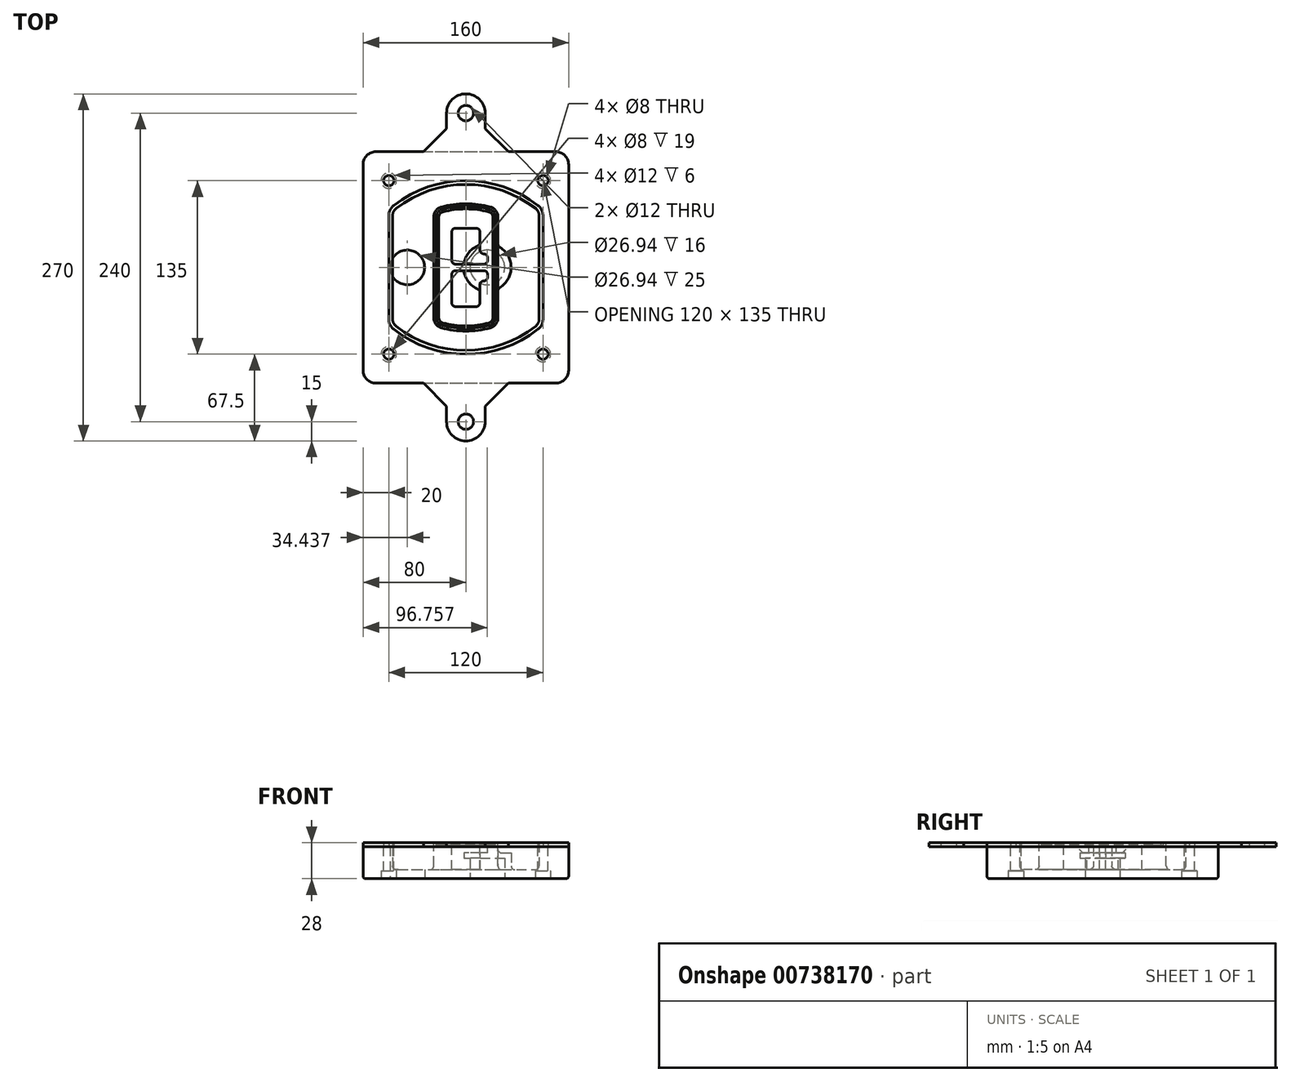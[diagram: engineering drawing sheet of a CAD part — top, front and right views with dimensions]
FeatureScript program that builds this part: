
annotation { "Feature Type Name" : "Feature", "Feature Type Description" : "" }
export const myFeature = defineFeature(function(context is Context, id is Id, definition is map)
    precondition{}
    {
        {
            var Q0;
            Q0=qCreatedBy(makeId("Top.planeOp"),FACE);
            var sketch = newSketch(context, id + "F0", { "sketchPlane" : qUnion([Q0])});
            skPoint(sketch, "E0.rect.middle", {"position": v(0, 0) * mm});
            skLineSegment(sketch, "E1.bottom", {"start": v(-70, -90) * mm, "end": v(70, -90) * mm});
            skLineSegment(sketch, "E1.top", {"start": v(-70, 90) * mm, "end": v(70, 90) * mm});
            skLineSegment(sketch, "E1.left", {"start": v(-80, -80) * mm, "end": v(-80, 80) * mm});
            skLineSegment(sketch, "E1.right", {"start": v(80, -80) * mm, "end": v(80, 80) * mm});
            skLineSegment(sketch, "E2", {"start": v(-80, 90) * mm, "end": v(80, -90) * mm, "construction": true});
            skLineSegment(sketch, "E3", {"start": v(80, 90) * mm, "end": v(-80, -90) * mm, "construction": true});
            skCircle(sketch, "E4", {"center": v(-60, 67.5) * mm, "radius": 4 * mm});
            skCircle(sketch, "E5", {"center": v(60, 67.5) * mm, "radius": 4 * mm});
            skCircle(sketch, "E6", {"center": v(60, -67.5) * mm, "radius": 4 * mm});
            skCircle(sketch, "E7", {"center": v(-60, -67.5) * mm, "radius": 4 * mm});
            skLineSegment(sketch, "E8", {"start": v(-60, 67.5) * mm, "end": v(60, 67.5) * mm, "construction": true});
            skLineSegment(sketch, "E9", {"start": v(60, 67.5) * mm, "end": v(60, -67.5) * mm, "construction": true});
            skLineSegment(sketch, "E10", {"start": v(60, -67.5) * mm, "end": v(-60, -67.5) * mm, "construction": true});
            skLineSegment(sketch, "E11", {"start": v(-60, -67.5) * mm, "end": v(-60, 67.5) * mm, "construction": true});
            skLineSegment(sketch, "E12", {"start": v(-60, 40.3) * mm, "end": v(-60, -40.3) * mm});
            skLineSegment(sketch, "E13", {"start": v(60, 40.3) * mm, "end": v(60, -40.3) * mm});
            skArc(sketch, "E14", {"start": v(56.15, 48.18) * mm, "mid": v(0, 67.5) * mm, "end": v(-56.15, 48.18) * mm});
            skArc(sketch, "E15", {"start": v(-56.15, -48.18) * mm, "mid": v(0, -67.5) * mm, "end": v(56.15, -48.18) * mm});
            skLineSegment(sketch, "E16", {"start": v(-60, 0) * mm, "end": v(60, 0) * mm, "construction": true});
            skPoint(sketch, "E17.visualSharp", {"position": v(-60, -45) * mm});
            skArc(sketch, "E17.filletArc", {"start": v(-60, -40.3) * mm, "mid": v(-58.99, -44.68) * mm, "end": v(-56.15, -48.18) * mm});
            skPoint(sketch, "E18.visualSharp", {"position": v(-60, 45) * mm});
            skArc(sketch, "E18.filletArc", {"start": v(-56.15, 48.18) * mm, "mid": v(-58.99, 44.68) * mm, "end": v(-60, 40.3) * mm});
            skPoint(sketch, "E19.visualSharp", {"position": v(60, 45) * mm});
            skArc(sketch, "E19.filletArc", {"start": v(60, 40.3) * mm, "mid": v(58.99, 44.68) * mm, "end": v(56.15, 48.18) * mm});
            skPoint(sketch, "E20.visualSharp", {"position": v(60, -45) * mm});
            skArc(sketch, "E20.filletArc", {"start": v(56.15, -48.18) * mm, "mid": v(58.99, -44.68) * mm, "end": v(60, -40.3) * mm});
            skPoint(sketch, "E21.visualSharp", {"position": v(-80, 90) * mm});
            skArc(sketch, "E21.filletArc", {"start": v(-70, 90) * mm, "mid": v(-77.07, 87.07) * mm, "end": v(-80, 80) * mm});
            skPoint(sketch, "E22.visualSharp", {"position": v(80, 90) * mm});
            skArc(sketch, "E22.filletArc", {"start": v(80, 80) * mm, "mid": v(77.07, 87.07) * mm, "end": v(70, 90) * mm});
            skPoint(sketch, "E23.visualSharp", {"position": v(80, -90) * mm});
            skArc(sketch, "E23.filletArc", {"start": v(70, -90) * mm, "mid": v(77.07, -87.07) * mm, "end": v(80, -80) * mm});
            skPoint(sketch, "E24.visualSharp", {"position": v(-80, -90) * mm});
            skArc(sketch, "E24.filletArc", {"start": v(-80, -80) * mm, "mid": v(-77.07, -87.07) * mm, "end": v(-70, -90) * mm});
            skArc(sketch, "E25.0", {"start": v(57, 40.3) * mm, "mid": v(56.3, 43.36) * mm, "end": v(54.3, 45.81) * mm});
            skLineSegment(sketch, "E25.1", {"start": v(57, 40.3) * mm, "end": v(57, -40.3) * mm});
            skArc(sketch, "E25.2", {"start": v(54.3, -45.81) * mm, "mid": v(56.3, -43.36) * mm, "end": v(57, -40.3) * mm});
            skArc(sketch, "E25.3", {"start": v(-54.3, -45.81) * mm, "mid": v(0, -64.5) * mm, "end": v(54.3, -45.81) * mm});
            skArc(sketch, "E25.4", {"start": v(-57, -40.3) * mm, "mid": v(-56.3, -43.36) * mm, "end": v(-54.3, -45.81) * mm});
            skArc(sketch, "E25.5", {"start": v(54.3, 45.81) * mm, "mid": v(0, 64.5) * mm, "end": v(-54.3, 45.81) * mm});
            skLineSegment(sketch, "E25.6", {"start": v(-57, 40.3) * mm, "end": v(-57, -40.3) * mm});
            skArc(sketch, "E25.7", {"start": v(-54.3, 45.81) * mm, "mid": v(-56.3, 43.36) * mm, "end": v(-57, 40.3) * mm});
            skArc(sketch, "E26.0", {"start": v(-58.62, 51.33) * mm, "mid": v(-62.58, 46.43) * mm, "end": v(-64, 40.3) * mm});
            skArc(sketch, "E26.1", {"start": v(58.62, 51.33) * mm, "mid": v(0, 71.5) * mm, "end": v(-58.62, 51.33) * mm});
            skArc(sketch, "E26.2", {"start": v(64, 40.3) * mm, "mid": v(62.58, 46.43) * mm, "end": v(58.62, 51.33) * mm});
            skLineSegment(sketch, "E26.3", {"start": v(64, 40.3) * mm, "end": v(64, -40.3) * mm});
            skArc(sketch, "E26.4", {"start": v(58.62, -51.33) * mm, "mid": v(62.58, -46.43) * mm, "end": v(64, -40.3) * mm});
            skLineSegment(sketch, "E26.5", {"start": v(-64, 40.3) * mm, "end": v(-64, -40.3) * mm});
            skArc(sketch, "E26.6", {"start": v(-58.62, -51.33) * mm, "mid": v(0, -71.5) * mm, "end": v(58.62, -51.33) * mm});
            skArc(sketch, "E26.7", {"start": v(-64, -40.3) * mm, "mid": v(-62.58, -46.43) * mm, "end": v(-58.62, -51.33) * mm});
            skSolve(sketch);
        }
        {
            var Q0;
            Q0=makeQuery(id+"F0.imprint","IMPRINT",FACE,{"disambiguationData":[TD([[makeQuery(id+"F0.imprint","IMPRINT",EDGE,{"derivedFrom":sQuery(id+"F0.wireOp",EDGE,"E1.bottom")}),1.0]])]});
            var Q1;
            Q1=makeQuery(id+"F0.imprint","IMPRINT",FACE,{"disambiguationData":[TD([[makeQuery(id+"F0.imprint","IMPRINT",EDGE,{"derivedFrom":sQuery(id+"F0.wireOp",EDGE,"E12")}),1.0]])]});
            var Q2;
            Q2=makeQuery(id+"F0.imprint","IMPRINT",FACE,{"disambiguationData":[TD([[makeQuery(id+"F0.imprint","IMPRINT",EDGE,{"derivedFrom":sQuery(id+"F0.wireOp",EDGE,"E25.0")}),1.0]])]});
            var Q3;
            Q3=makeQuery(id+"F0.imprint","IMPRINT",FACE,{"disambiguationData":[TD([[makeQuery(id+"F0.imprint","IMPRINT",EDGE,{"derivedFrom":sQuery(id+"F0.wireOp",EDGE,"E12")}),-1.0]])]});
            extrude(context, id + "F1", {"entities" : qUnion([Q0, Q1, Q2, Q3]), "oppositeDirection" : true, "depth" : 25 * mm});
        }
        {
            var Q0;
            Q0=makeQuery(id+"F0.imprint","IMPRINT",FACE,{"disambiguationData":[TD([[makeQuery(id+"F0.imprint","IMPRINT",EDGE,{"derivedFrom":sQuery(id+"F0.wireOp",EDGE,"E12")}),1.0]])]});
            extrude(context, id + "F2", {"entities" : qUnion([Q0]), "operationType" : NewBodyOperationType.ADD, "depth" : 3 * mm, "offsetDistance" : 25 * mm});
        }
        {
            var Q0;
            Q0=makeQuery(id+"F0.imprint","IMPRINT",FACE,{"disambiguationData":[TD([[makeQuery(id+"F0.imprint","IMPRINT",EDGE,{"derivedFrom":sQuery(id+"F0.wireOp",EDGE,"E25.0")}),1.0]])]});
            extrude(context, id + "F3", {"entities" : qUnion([Q0]), "operationType" : NewBodyOperationType.REMOVE, "oppositeDirection" : true, "depth" : 18 * mm});
        }
        {
            var Q0;
            Q0=makeQuery(id+"F2.opExtrude","CAP_FACE",FACE,{"disambiguationData":[OSD([sQuery(id+"F0.wireOp",EDGE,"E12"),sQuery(id+"F0.wireOp",EDGE,"E13"),sQuery(id+"F0.wireOp",EDGE,"E14"),sQuery(id+"F0.wireOp",EDGE,"E15"),sQuery(id+"F0.wireOp",EDGE,"E17.filletArc"),sQuery(id+"F0.wireOp",EDGE,"E18.filletArc"),sQuery(id+"F0.wireOp",EDGE,"E19.filletArc"),sQuery(id+"F0.wireOp",EDGE,"E20.filletArc"),sQuery(id+"F0.wireOp",EDGE,"E25.0"),sQuery(id+"F0.wireOp",EDGE,"E25.1"),sQuery(id+"F0.wireOp",EDGE,"E25.2"),sQuery(id+"F0.wireOp",EDGE,"E25.3"),sQuery(id+"F0.wireOp",EDGE,"E25.4"),sQuery(id+"F0.wireOp",EDGE,"E25.5"),sQuery(id+"F0.wireOp",EDGE,"E25.6"),sQuery(id+"F0.wireOp",EDGE,"E25.7")])],"isStart":false});
            var sketch = newSketch(context, id + "F4", { "sketchPlane" : qUnion([Q0])});
            skArc(sketch, "E27.0", {"start": v(-19.08, -46.97) * mm, "mid": v(0, -49.5) * mm, "end": v(19.08, -46.97) * mm});
            skArc(sketch, "E28.0", {"start": v(19.08, 46.97) * mm, "mid": v(0, 49.5) * mm, "end": v(-19.08, 46.97) * mm});
            skLineSegment(sketch, "E29", {"start": v(-25, 39.25) * mm, "end": v(-25, -39.25) * mm});
            skLineSegment(sketch, "E30", {"start": v(25, 39.25) * mm, "end": v(25, -39.25) * mm});
            skLineSegment(sketch, "E31", {"start": v(-25, 45.1) * mm, "end": v(25, 45.1) * mm, "construction": true});
            skLineSegment(sketch, "E32", {"start": v(-25, -45.1) * mm, "end": v(25, -45.1) * mm, "construction": true});
            skPoint(sketch, "E33.visualSharp", {"position": v(-25, 45.1) * mm});
            skArc(sketch, "E33.filletArc", {"start": v(-19.08, 46.97) * mm, "mid": v(-23.35, 44.11) * mm, "end": v(-25, 39.25) * mm});
            skPoint(sketch, "E34.visualSharp", {"position": v(25, 45.1) * mm});
            skArc(sketch, "E34.filletArc", {"start": v(25, 39.25) * mm, "mid": v(23.35, 44.11) * mm, "end": v(19.08, 46.97) * mm});
            skPoint(sketch, "E35.visualSharp", {"position": v(25, -45.1) * mm});
            skArc(sketch, "E35.filletArc", {"start": v(19.08, -46.97) * mm, "mid": v(23.35, -44.11) * mm, "end": v(25, -39.25) * mm});
            skPoint(sketch, "E36.visualSharp", {"position": v(-25, -45.1) * mm});
            skArc(sketch, "E36.filletArc", {"start": v(-25, -39.25) * mm, "mid": v(-23.35, -44.11) * mm, "end": v(-19.08, -46.97) * mm});
            skArc(sketch, "E37.0", {"start": v(54.3, 45.81) * mm, "mid": v(0, 64.5) * mm, "end": v(-54.3, 45.81) * mm});
            skArc(sketch, "E37.1", {"start": v(-54.3, 45.81) * mm, "mid": v(-56.3, 43.36) * mm, "end": v(-57, 40.3) * mm});
            skLineSegment(sketch, "E37.2", {"start": v(-57, 40.3) * mm, "end": v(-57, -40.3) * mm});
            skArc(sketch, "E37.3", {"start": v(-57, -40.3) * mm, "mid": v(-56.3, -43.36) * mm, "end": v(-54.3, -45.81) * mm});
            skArc(sketch, "E37.4", {"start": v(-54.3, -45.81) * mm, "mid": v(0, -64.5) * mm, "end": v(54.3, -45.81) * mm});
            skArc(sketch, "E37.5", {"start": v(54.3, -45.81) * mm, "mid": v(56.3, -43.36) * mm, "end": v(57, -40.3) * mm});
            skLineSegment(sketch, "E37.6", {"start": v(57, 40.3) * mm, "end": v(57, -40.3) * mm});
            skArc(sketch, "E37.7", {"start": v(57, 40.3) * mm, "mid": v(56.3, 43.36) * mm, "end": v(54.3, 45.81) * mm});
            skLineSegment(sketch, "E38.0", {"start": v(23, 39.25) * mm, "end": v(23, -39.25) * mm});
            skArc(sketch, "E38.1", {"start": v(18.56, -45.04) * mm, "mid": v(21.76, -42.9) * mm, "end": v(23, -39.25) * mm});
            skArc(sketch, "E38.2", {"start": v(-18.56, -45.04) * mm, "mid": v(0, -47.5) * mm, "end": v(18.56, -45.04) * mm});
            skArc(sketch, "E38.3", {"start": v(-23, -39.25) * mm, "mid": v(-21.76, -42.9) * mm, "end": v(-18.56, -45.04) * mm});
            skLineSegment(sketch, "E38.4", {"start": v(-23, 39.25) * mm, "end": v(-23, -39.25) * mm});
            skArc(sketch, "E38.5", {"start": v(23, 39.25) * mm, "mid": v(21.76, 42.9) * mm, "end": v(18.56, 45.04) * mm});
            skArc(sketch, "E38.6", {"start": v(-18.56, 45.04) * mm, "mid": v(-21.76, 42.9) * mm, "end": v(-23, 39.25) * mm});
            skArc(sketch, "E38.7", {"start": v(18.56, 45.04) * mm, "mid": v(0, 47.5) * mm, "end": v(-18.56, 45.04) * mm});
            skArc(sketch, "E39.0", {"start": v(21, 39.25) * mm, "mid": v(20.18, 41.68) * mm, "end": v(18.04, 43.1) * mm});
            skLineSegment(sketch, "E39.1", {"start": v(21, 39.25) * mm, "end": v(21, -39.25) * mm});
            skArc(sketch, "E39.2", {"start": v(18.04, -43.1) * mm, "mid": v(20.18, -41.68) * mm, "end": v(21, -39.25) * mm});
            skArc(sketch, "E39.3", {"start": v(-18.04, -43.1) * mm, "mid": v(0, -45.5) * mm, "end": v(18.04, -43.1) * mm});
            skArc(sketch, "E39.4", {"start": v(-21, -39.25) * mm, "mid": v(-20.18, -41.68) * mm, "end": v(-18.04, -43.1) * mm});
            skArc(sketch, "E39.5", {"start": v(18.04, 43.1) * mm, "mid": v(0, 45.5) * mm, "end": v(-18.04, 43.1) * mm});
            skLineSegment(sketch, "E39.6", {"start": v(-21, 39.25) * mm, "end": v(-21, -39.25) * mm});
            skArc(sketch, "E39.7", {"start": v(-18.04, 43.1) * mm, "mid": v(-20.18, 41.68) * mm, "end": v(-21, 39.25) * mm});
            skLineSegment(sketch, "E40", {"start": v(-25, 0) * mm, "end": v(25, 0) * mm, "construction": true});
            skLineSegment(sketch, "E41", {"start": v(-11, 5.5) * mm, "end": v(-11, 27.5) * mm});
            skLineSegment(sketch, "E42", {"start": v(-8, 30.5) * mm, "end": v(8, 30.5) * mm});
            skLineSegment(sketch, "E43", {"start": v(11, 27.5) * mm, "end": v(11, 13.5) * mm});
            skLineSegment(sketch, "E44", {"start": v(14, 10.5) * mm, "end": v(14, 10.5) * mm});
            skLineSegment(sketch, "E45", {"start": v(17, 7.5) * mm, "end": v(17, 5.5) * mm});
            skLineSegment(sketch, "E46", {"start": v(14, 2.5) * mm, "end": v(-8, 2.5) * mm});
            skPoint(sketch, "E47.visualSharp", {"position": v(-11, 30.5) * mm});
            skArc(sketch, "E47.filletArc", {"start": v(-8, 30.5) * mm, "mid": v(-10.12, 29.62) * mm, "end": v(-11, 27.5) * mm});
            skPoint(sketch, "E48.visualSharp", {"position": v(11, 30.5) * mm});
            skArc(sketch, "E48.filletArc", {"start": v(11, 27.5) * mm, "mid": v(10.12, 29.62) * mm, "end": v(8, 30.5) * mm});
            skPoint(sketch, "E49.visualSharp", {"position": v(11, 10.5) * mm});
            skArc(sketch, "E49.filletArc", {"start": v(11, 13.5) * mm, "mid": v(11.88, 11.38) * mm, "end": v(14, 10.5) * mm});
            skPoint(sketch, "E50.visualSharp", {"position": v(17, 10.5) * mm});
            skArc(sketch, "E50.filletArc", {"start": v(17, 7.5) * mm, "mid": v(16.12, 9.62) * mm, "end": v(14, 10.5) * mm});
            skPoint(sketch, "E51.visualSharp", {"position": v(17, 2.5) * mm});
            skArc(sketch, "E51.filletArc", {"start": v(14, 2.5) * mm, "mid": v(16.12, 3.38) * mm, "end": v(17, 5.5) * mm});
            skPoint(sketch, "E52.visualSharp", {"position": v(-11, 2.5) * mm});
            skArc(sketch, "E52.filletArc", {"start": v(-11, 5.5) * mm, "mid": v(-10.12, 3.38) * mm, "end": v(-8, 2.5) * mm});
            skLineSegment(sketch, "E53.0.MirrorCS", {"start": v(14, -2.5) * mm, "end": v(-8, -2.5) * mm});
            skArc(sketch, "E54.0.MirrorCS", {"start": v(-11, -5.5) * mm, "mid": v(-10.12, -3.38) * mm, "end": v(-8, -2.5) * mm});
            skLineSegment(sketch, "E55.0.MirrorCS", {"start": v(-11, -5.5) * mm, "end": v(-11, -27.5) * mm});
            skArc(sketch, "E56.0.MirrorCS", {"start": v(-8, -30.5) * mm, "mid": v(-10.12, -29.62) * mm, "end": v(-11, -27.5) * mm});
            skLineSegment(sketch, "E57.0.MirrorCS", {"start": v(-8, -30.5) * mm, "end": v(8, -30.5) * mm});
            skArc(sketch, "E58.0.MirrorCS", {"start": v(11, -27.5) * mm, "mid": v(10.12, -29.62) * mm, "end": v(8, -30.5) * mm});
            skLineSegment(sketch, "E59.0.MirrorCS", {"start": v(11, -27.5) * mm, "end": v(11, -13.5) * mm});
            skArc(sketch, "E60.0.MirrorCS", {"start": v(11, -13.5) * mm, "mid": v(11.88, -11.38) * mm, "end": v(14, -10.5) * mm});
            skArc(sketch, "E61.0.MirrorCS", {"start": v(17, -7.5) * mm, "mid": v(16.12, -9.62) * mm, "end": v(14, -10.5) * mm});
            skLineSegment(sketch, "E62.0.MirrorCS", {"start": v(17, -7.5) * mm, "end": v(17, -5.5) * mm});
            skArc(sketch, "E63.0.MirrorCS", {"start": v(14, -2.5) * mm, "mid": v(16.12, -3.38) * mm, "end": v(17, -5.5) * mm});
            skSolve(sketch);
        }
        {
            var Q0;
            Q0=makeQuery(id+"F4.imprint","IMPRINT",FACE,{"disambiguationData":[TD([[makeQuery(id+"F4.imprint","IMPRINT",EDGE,{"derivedFrom":sQuery(id+"F4.wireOp",EDGE,"E27.0")}),1.0]])]});
            var Q1;
            Q1=makeQuery(id+"F4.imprint","IMPRINT",FACE,{"disambiguationData":[TD([[makeQuery(id+"F4.imprint","IMPRINT",EDGE,{"derivedFrom":sQuery(id+"F4.wireOp",EDGE,"E38.0")}),-1.0]])]});
            var Q2;
            Q2=makeQuery(id+"F4.imprint","IMPRINT",FACE,{"disambiguationData":[TD([[makeQuery(id+"F4.imprint","IMPRINT",EDGE,{"derivedFrom":sQuery(id+"F4.wireOp",EDGE,"E39.0")}),1.0]])]});
            extrude(context, id + "F5", {"entities" : qUnion([Q0, Q1, Q2]), "operationType" : NewBodyOperationType.ADD, "endBound" : BoundingType.UP_TO_NEXT, "oppositeDirection" : true, "depth" : 25 * mm});
        }
        {
            var Q0;
            Q0=makeQuery(id+"F4.imprint","IMPRINT",FACE,{"disambiguationData":[TD([[makeQuery(id+"F4.imprint","IMPRINT",EDGE,{"derivedFrom":sQuery(id+"F4.wireOp",EDGE,"E38.0")}),-1.0]])]});
            extrude(context, id + "F6", {"entities" : qUnion([Q0]), "operationType" : NewBodyOperationType.REMOVE, "oppositeDirection" : true, "depth" : 2 * mm});
        }
        {
            var Q0;
            Q0=makeQuery(id+"F1.opExtrude","CAP_FACE",FACE,{"disambiguationData":[OSD([sQuery(id+"F0.wireOp",EDGE,"E1.bottom"),sQuery(id+"F0.wireOp",EDGE,"E1.top"),sQuery(id+"F0.wireOp",EDGE,"E1.left"),sQuery(id+"F0.wireOp",EDGE,"E1.right"),sQuery(id+"F0.wireOp",EDGE,"E4"),sQuery(id+"F0.wireOp",EDGE,"E5"),sQuery(id+"F0.wireOp",EDGE,"E6"),sQuery(id+"F0.wireOp",EDGE,"E7"),sQuery(id+"F0.wireOp",EDGE,"E21.filletArc"),sQuery(id+"F0.wireOp",EDGE,"E22.filletArc"),sQuery(id+"F0.wireOp",EDGE,"E23.filletArc"),sQuery(id+"F0.wireOp",EDGE,"E24.filletArc")])],"isStart":false});
            var sketch = newSketch(context, id + "F7", { "sketchPlane" : qUnion([Q0])});
            skCircle(sketch, "E64", {"center": v(16.76, 0) * mm, "radius": 13.47 * mm});
            skCircle(sketch, "E65", {"center": v(-45.56, 0) * mm, "radius": 13.47 * mm});
            skLineSegment(sketch, "E66", {"start": v(80, 0) * mm, "end": v(-80, 0) * mm});
            skCircle(sketch, "E67", {"center": v(16.76, 0) * mm, "radius": 18.47 * mm});
            skCircle(sketch, "E68", {"center": v(60, -67.5) * mm, "radius": 6 * mm});
            skCircle(sketch, "E69", {"center": v(-60, -67.5) * mm, "radius": 6 * mm});
            skCircle(sketch, "E70", {"center": v(-60, 67.5) * mm, "radius": 6 * mm});
            skCircle(sketch, "E71", {"center": v(60, 67.5) * mm, "radius": 6 * mm});
            skSolve(sketch);
        }
        {
            var Q0;
            {var subQ1=sQuery(id+"F7.wireOp",EDGE,"E66");var subQ4=sQuery(id+"F7.wireOp",EDGE,"E64");var subQ6=makeQuery(id+"F7.imprint","INTERSECT",VERTEX,{"disambiguationData":[OD(0.0)],"derivedFrom":[subQ4,subQ1]});Q0=makeQuery(id+"F7.imprint","IMPRINT",FACE,{"disambiguationData":[TD([[makeQuery(id+"F7.imprint","IMPRINT",EDGE,{"disambiguationData":[TD([[subQ6,-1.0]])],"derivedFrom":subQ4}),-1.0]])]});}
            var Q1;
            {var subQ0=sQuery(id+"F7.wireOp",EDGE,"E66");var subQ1=sQuery(id+"F7.wireOp",EDGE,"E64");var subQ3=makeQuery(id+"F7.imprint","INTERSECT",VERTEX,{"disambiguationData":[OD(0.0)],"derivedFrom":[subQ1,subQ0]});Q1=makeQuery(id+"F7.imprint","IMPRINT",FACE,{"disambiguationData":[TD([[makeQuery(id+"F7.imprint","IMPRINT",EDGE,{"disambiguationData":[TD([[subQ3,-1.0]])],"derivedFrom":subQ1}),1.0]])]});}
            var Q2;
            {var subQ0=sQuery(id+"F7.wireOp",EDGE,"E66");var subQ1=sQuery(id+"F7.wireOp",EDGE,"E64");var subQ3=makeQuery(id+"F7.imprint","INTERSECT",VERTEX,{"disambiguationData":[OD(0.0)],"derivedFrom":[subQ1,subQ0]});Q2=makeQuery(id+"F7.imprint","IMPRINT",FACE,{"disambiguationData":[TD([[makeQuery(id+"F7.imprint","IMPRINT",EDGE,{"disambiguationData":[TD([[subQ3,1.0]])],"derivedFrom":subQ1}),1.0]])]});}
            var Q3;
            {var subQ1=sQuery(id+"F7.wireOp",EDGE,"E66");var subQ4=sQuery(id+"F7.wireOp",EDGE,"E64");var subQ6=makeQuery(id+"F7.imprint","INTERSECT",VERTEX,{"disambiguationData":[OD(0.0)],"derivedFrom":[subQ4,subQ1]});Q3=makeQuery(id+"F7.imprint","IMPRINT",FACE,{"disambiguationData":[TD([[makeQuery(id+"F7.imprint","IMPRINT",EDGE,{"disambiguationData":[TD([[subQ6,1.0]])],"derivedFrom":subQ4}),-1.0]])]});}
            extrude(context, id + "F8", {"entities" : qUnion([Q0, Q1, Q2, Q3]), "operationType" : NewBodyOperationType.ADD, "oppositeDirection" : true, "depth" : 20 * mm});
        }
        {
            var Q0;
            {var subQ0=sQuery(id+"F7.wireOp",EDGE,"E66");var subQ1=sQuery(id+"F7.wireOp",EDGE,"E64");var subQ3=makeQuery(id+"F7.imprint","INTERSECT",VERTEX,{"disambiguationData":[OD(0.0)],"derivedFrom":[subQ1,subQ0]});Q0=makeQuery(id+"F7.imprint","IMPRINT",FACE,{"disambiguationData":[TD([[makeQuery(id+"F7.imprint","IMPRINT",EDGE,{"disambiguationData":[TD([[subQ3,-1.0]])],"derivedFrom":subQ1}),1.0]])]});}
            var Q1;
            {var subQ0=sQuery(id+"F7.wireOp",EDGE,"E66");var subQ1=sQuery(id+"F7.wireOp",EDGE,"E64");var subQ3=makeQuery(id+"F7.imprint","INTERSECT",VERTEX,{"disambiguationData":[OD(0.0)],"derivedFrom":[subQ1,subQ0]});Q1=makeQuery(id+"F7.imprint","IMPRINT",FACE,{"disambiguationData":[TD([[makeQuery(id+"F7.imprint","IMPRINT",EDGE,{"disambiguationData":[TD([[subQ3,1.0]])],"derivedFrom":subQ1}),1.0]])]});}
            extrude(context, id + "F9", {"entities" : qUnion([Q0, Q1]), "operationType" : NewBodyOperationType.REMOVE, "oppositeDirection" : true, "depth" : 16 * mm});
        }
        {
            var Q0;
            {var subQ0=sQuery(id+"F7.wireOp",EDGE,"E66");var subQ1=sQuery(id+"F7.wireOp",EDGE,"E65");var subQ3=makeQuery(id+"F7.imprint","INTERSECT",VERTEX,{"disambiguationData":[OD(0.0)],"derivedFrom":[subQ1,subQ0]});Q0=makeQuery(id+"F7.imprint","IMPRINT",FACE,{"disambiguationData":[TD([[makeQuery(id+"F7.imprint","IMPRINT",EDGE,{"disambiguationData":[TD([[subQ3,-1.0]])],"derivedFrom":subQ1}),1.0]])]});}
            var Q1;
            {var subQ0=sQuery(id+"F7.wireOp",EDGE,"E66");var subQ1=sQuery(id+"F7.wireOp",EDGE,"E65");var subQ3=makeQuery(id+"F7.imprint","INTERSECT",VERTEX,{"disambiguationData":[OD(0.0)],"derivedFrom":[subQ1,subQ0]});Q1=makeQuery(id+"F7.imprint","IMPRINT",FACE,{"disambiguationData":[TD([[makeQuery(id+"F7.imprint","IMPRINT",EDGE,{"disambiguationData":[TD([[subQ3,1.0]])],"derivedFrom":subQ1}),1.0]])]});}
            extrude(context, id + "F10", {"entities" : qUnion([Q0, Q1]), "operationType" : NewBodyOperationType.REMOVE, "oppositeDirection" : true, "depth" : 25 * mm, "offsetDistance" : 25 * mm});
        }
        {
            var Q0;
            Q0=makeQuery(id+"F7.imprint","IMPRINT",FACE,{"disambiguationData":[TD([[makeQuery(id+"F7.imprint","IMPRINT",EDGE,{"derivedFrom":sQuery(id+"F7.wireOp",EDGE,"E68")}),1.0]])]});
            var Q1;
            Q1=makeQuery(id+"F7.imprint","IMPRINT",FACE,{"disambiguationData":[TD([[makeQuery(id+"F7.imprint","IMPRINT",EDGE,{"derivedFrom":makeQuery(id+"F1.opExtrude","CAP_EDGE",EDGE,{"disambiguationData":[OSD([sQuery(id+"F0.wireOp",EDGE,"E5")])],"isStart":false})}),-1.0]])]});
            var Q2;
            Q2=makeQuery(id+"F7.imprint","IMPRINT",FACE,{"disambiguationData":[TD([[makeQuery(id+"F7.imprint","IMPRINT",EDGE,{"derivedFrom":sQuery(id+"F7.wireOp",EDGE,"E69")}),1.0]])]});
            var Q3;
            Q3=makeQuery(id+"F7.imprint","IMPRINT",FACE,{"disambiguationData":[TD([[makeQuery(id+"F7.imprint","IMPRINT",EDGE,{"derivedFrom":makeQuery(id+"F1.opExtrude","CAP_EDGE",EDGE,{"disambiguationData":[OSD([sQuery(id+"F0.wireOp",EDGE,"E4")])],"isStart":false})}),-1.0]])]});
            var Q4;
            Q4=makeQuery(id+"F7.imprint","IMPRINT",FACE,{"disambiguationData":[TD([[makeQuery(id+"F7.imprint","IMPRINT",EDGE,{"derivedFrom":sQuery(id+"F7.wireOp",EDGE,"E70")}),1.0]])]});
            var Q5;
            Q5=makeQuery(id+"F7.imprint","IMPRINT",FACE,{"disambiguationData":[TD([[makeQuery(id+"F7.imprint","IMPRINT",EDGE,{"derivedFrom":makeQuery(id+"F1.opExtrude","CAP_EDGE",EDGE,{"disambiguationData":[OSD([sQuery(id+"F0.wireOp",EDGE,"E7")])],"isStart":false})}),-1.0]])]});
            var Q6;
            Q6=makeQuery(id+"F7.imprint","IMPRINT",FACE,{"disambiguationData":[TD([[makeQuery(id+"F7.imprint","IMPRINT",EDGE,{"derivedFrom":sQuery(id+"F7.wireOp",EDGE,"E71")}),1.0]])]});
            var Q7;
            Q7=makeQuery(id+"F7.imprint","IMPRINT",FACE,{"disambiguationData":[TD([[makeQuery(id+"F7.imprint","IMPRINT",EDGE,{"derivedFrom":makeQuery(id+"F1.opExtrude","CAP_EDGE",EDGE,{"disambiguationData":[OSD([sQuery(id+"F0.wireOp",EDGE,"E6")])],"isStart":false})}),-1.0]])]});
            extrude(context, id + "F11", {"entities" : qUnion([Q0, Q1, Q2, Q3, Q4, Q5, Q6, Q7]), "operationType" : NewBodyOperationType.REMOVE, "oppositeDirection" : true, "depth" : 6 * mm});
        }
        {
            var Q0;
            Q0=makeQuery(id+"F9.boolean.opBoolean","COPY",FACE,{"derivedFrom":makeQuery(id+"F9.opExtrude","CAP_FACE",FACE,{"disambiguationData":[OSD([sQuery(id+"F7.wireOp",EDGE,"E64")])],"isStart":false})});
            var sketch = newSketch(context, id + "F12", { "sketchPlane" : qUnion([Q0])});
            skArc(sketch, "E72.0", {"start": v(11, 17.55) * mm, "mid": v(2.57, 11.82) * mm, "end": v(-1.54, 2.5) * mm});
            skArc(sketch, "E72.1", {"start": v(-1.54, -2.5) * mm, "mid": v(2.57, -11.82) * mm, "end": v(11, -17.55) * mm});
            skLineSegment(sketch, "E73", {"start": v(-1.54, -2.5) * mm, "end": v(14, -2.5) * mm});
            skLineSegment(sketch, "E74.0", {"start": v(14, 2.5) * mm, "end": v(-1.54, 2.5) * mm});
            skArc(sketch, "E74.1", {"start": v(14, 2.5) * mm, "mid": v(16.12, 3.38) * mm, "end": v(17, 5.5) * mm});
            skLineSegment(sketch, "E74.2", {"start": v(17, 7.5) * mm, "end": v(17, 5.5) * mm});
            skArc(sketch, "E74.3", {"start": v(17, 7.5) * mm, "mid": v(16.12, 9.62) * mm, "end": v(14, 10.5) * mm});
            skArc(sketch, "E74.4", {"start": v(11, 13.5) * mm, "mid": v(11.88, 11.38) * mm, "end": v(14, 10.5) * mm});
            skLineSegment(sketch, "E74.5", {"start": v(11, 17.55) * mm, "end": v(11, 13.5) * mm});
            skLineSegment(sketch, "E74.7", {"start": v(14, -2.5) * mm, "end": v(-1.54, -2.5) * mm});
            skArc(sketch, "E74.8", {"start": v(14, -2.5) * mm, "mid": v(16.12, -3.38) * mm, "end": v(17, -5.5) * mm});
            skLineSegment(sketch, "E74.9", {"start": v(17, -7.5) * mm, "end": v(17, -5.5) * mm});
            skArc(sketch, "E74.10", {"start": v(17, -7.5) * mm, "mid": v(16.12, -9.62) * mm, "end": v(14, -10.5) * mm});
            skArc(sketch, "E74.11", {"start": v(11, -13.5) * mm, "mid": v(11.88, -11.38) * mm, "end": v(14, -10.5) * mm});
            skLineSegment(sketch, "E74.12", {"start": v(11, -17.55) * mm, "end": v(11, -13.5) * mm});
            skPoint(sketch, "E75.orphan", {"position": v(11, -27.5) * mm});
            skPoint(sketch, "E76.orphan", {"position": v(-8, -2.5) * mm});
            skPoint(sketch, "E77.orphan", {"position": v(-8, 2.5) * mm});
            skPoint(sketch, "E78.orphan", {"position": v(11, 27.5) * mm});
            skSolve(sketch);
        }
        {
            var Q0;
            {var subQ7=sQuery(id+"F12.wireOp",EDGE,"E72.0");var subQ14=sQuery(id+"F12.wireOp",EDGE,"E72.1");var subQ16=sQuery(id+"F12.wireOp",EDGE,"E74.1");var subQ18=sQuery(id+"F12.wireOp",EDGE,"E74.8");Q0=qUnion([makeQuery(id+"F12.imprint","IMPRINT",FACE,{"disambiguationData":[TD([[makeQuery(id+"F12.imprint","IMPRINT",EDGE,{"derivedFrom":subQ7}),1.0]])]}),makeQuery(id+"F12.imprint","IMPRINT",FACE,{"disambiguationData":[TD([[makeQuery(id+"F12.imprint","IMPRINT",EDGE,{"derivedFrom":subQ14}),1.0]])]}),makeQuery(id+"F12.imprint","IMPRINT",FACE,{"disambiguationData":[TD([[makeQuery(id+"F12.imprint","IMPRINT",EDGE,{"derivedFrom":subQ16}),1.0]])]}),makeQuery(id+"F12.imprint","IMPRINT",FACE,{"disambiguationData":[TD([[makeQuery(id+"F12.imprint","IMPRINT",EDGE,{"derivedFrom":subQ18}),-1.0]])]})]);}
            var Q1;
            Q1=makeQuery(id+"F5.boolean.opBoolean","SPLIT",FACE,{"disambiguationData":[TD([makeQuery(id+"F5.opExtrude","SWEPT_FACE",FACE,{"disambiguationData":[OSD([sQuery(id+"F4.wireOp",EDGE,"E41")])]})])],"derivedFrom":makeQuery(id+"F3.boolean.opBoolean","COPY",FACE,{"derivedFrom":makeQuery(id+"F3.opExtrude","CAP_FACE",FACE,{"disambiguationData":[OSD([sQuery(id+"F0.wireOp",EDGE,"E25.0"),sQuery(id+"F0.wireOp",EDGE,"E25.1"),sQuery(id+"F0.wireOp",EDGE,"E25.2"),sQuery(id+"F0.wireOp",EDGE,"E25.3"),sQuery(id+"F0.wireOp",EDGE,"E25.4"),sQuery(id+"F0.wireOp",EDGE,"E25.5"),sQuery(id+"F0.wireOp",EDGE,"E25.6"),sQuery(id+"F0.wireOp",EDGE,"E25.7")])],"isStart":false})})});
            extrude(context, id + "F13", {"entities" : qUnion([Q0]), "operationType" : NewBodyOperationType.REMOVE, "endBound" : BoundingType.UP_TO_SURFACE, "endBoundEntityFace" : qUnion([Q1]), "depth" : 25 * mm});
        }
        {
            var Q0;
            Q0=makeQuery(id+"F3.boolean.opBoolean","COPY",EDGE,{"derivedFrom":makeQuery(id+"F3.opExtrude","CAP_EDGE",EDGE,{"disambiguationData":[OSD([sQuery(id+"F0.wireOp",EDGE,"E25.6")])],"isStart":false})});
            var Q1;
            Q1=makeQuery(id+"F8.boolean.opBoolean","INTERSECT",EDGE,{"derivedFrom":[makeQuery(id+"F5.opExtrude","SWEPT_FACE",FACE,{"disambiguationData":[OSD([sQuery(id+"F4.wireOp",EDGE,"E30")])]}),makeQuery(id+"F8.opExtrude","CAP_FACE",FACE,{"disambiguationData":[OSD([sQuery(id+"F7.wireOp",EDGE,"E67")])],"isStart":false})]});
            var Q2;
            Q2=makeQuery(id+"F8.boolean.opBoolean","INTERSECT",EDGE,{"disambiguationData":[OD(1.0)],"derivedFrom":[makeQuery(id+"F5.opExtrude","SWEPT_FACE",FACE,{"disambiguationData":[OSD([sQuery(id+"F4.wireOp",EDGE,"E30")])]}),makeQuery(id+"F8.opExtrude","SWEPT_FACE",FACE,{"disambiguationData":[OSD([sQuery(id+"F7.wireOp",EDGE,"E67")])]})]});
            var Q3;
            {var subQ0=sQuery(id+"F4.wireOp",EDGE,"E30");Q3=makeQuery(id+"F8.boolean.opBoolean","SPLIT",EDGE,{"disambiguationData":[TD([makeQuery(id+"F5.opExtrude","SWEPT_FACE",FACE,{"disambiguationData":[OSD([sQuery(id+"F4.wireOp",EDGE,"E35.filletArc")])]})])],"derivedFrom":makeQuery(id+"F5.opExtrude","CAP_EDGE",EDGE,{"disambiguationData":[OSD([subQ0])],"isStart":false})});}
            var Q4;
            {var subQ0=sQuery(id+"F0.wireOp",EDGE,"E25.7");var subQ1=sQuery(id+"F0.wireOp",EDGE,"E25.1");var subQ2=sQuery(id+"F0.wireOp",EDGE,"E25.6");var subQ3=sQuery(id+"F0.wireOp",EDGE,"E25.5");var subQ4=sQuery(id+"F0.wireOp",EDGE,"E25.4");var subQ5=sQuery(id+"F0.wireOp",EDGE,"E25.0");var subQ6=sQuery(id+"F0.wireOp",EDGE,"E25.2");var subQ7=sQuery(id+"F0.wireOp",EDGE,"E25.3");Q4=makeQuery(id+"F8.boolean.opBoolean","INTERSECT",EDGE,{"derivedFrom":[makeQuery(id+"F5.boolean.opBoolean","SPLIT",FACE,{"disambiguationData":[TD([makeQuery(id+"F2.opExtrude","SWEPT_FACE",FACE,{"disambiguationData":[OSD([subQ5])]})])],"derivedFrom":makeQuery(id+"F3.boolean.opBoolean","COPY",FACE,{"derivedFrom":makeQuery(id+"F3.opExtrude","CAP_FACE",FACE,{"disambiguationData":[OSD([subQ5,subQ1,subQ6,subQ7,subQ4,subQ3,subQ2,subQ0])],"isStart":false})})}),makeQuery(id+"F8.opExtrude","SWEPT_FACE",FACE,{"disambiguationData":[OSD([sQuery(id+"F7.wireOp",EDGE,"E67")])]})]});}
            var Q5;
            Q5=makeQuery(id+"F8.boolean.opBoolean","INTERSECT",EDGE,{"disambiguationData":[OD(0.0)],"derivedFrom":[makeQuery(id+"F5.opExtrude","SWEPT_FACE",FACE,{"disambiguationData":[OSD([sQuery(id+"F4.wireOp",EDGE,"E30")])]}),makeQuery(id+"F8.opExtrude","SWEPT_FACE",FACE,{"disambiguationData":[OSD([sQuery(id+"F7.wireOp",EDGE,"E67")])]})]});
            fillet(context, id + "F14", {"entities" : qUnion([Q0, Q1, Q2, Q3, Q4, Q5]), "radius" : 3 * mm, "tangentPropagation" : true, "allowEdgeOverflow" : false});
        }
        {
            var Q0;
            Q0=makeQuery(id+"F1.opExtrude","CAP_EDGE",EDGE,{"disambiguationData":[OSD([sQuery(id+"F0.wireOp",EDGE,"E1.bottom")])],"isStart":false});
            fillet(context, id + "F15", {"entities" : qUnion([Q0]), "radius" : 2 * mm, "tangentPropagation" : true, "allowEdgeOverflow" : false});
        }
        {
            var Q0;
            {var subQ0=sQuery(id+"F0.wireOp",EDGE,"E21.filletArc");var subQ1=sQuery(id+"F0.wireOp",EDGE,"E7");var subQ2=sQuery(id+"F0.wireOp",EDGE,"E6");var subQ3=sQuery(id+"F0.wireOp",EDGE,"E5");var subQ4=sQuery(id+"F0.wireOp",EDGE,"E4");var subQ5=sQuery(id+"F0.wireOp",EDGE,"E22.filletArc");var subQ6=sQuery(id+"F0.wireOp",EDGE,"E1.bottom");var subQ7=sQuery(id+"F0.wireOp",EDGE,"E1.right");var subQ8=sQuery(id+"F0.wireOp",EDGE,"E1.top");var subQ9=sQuery(id+"F0.wireOp",EDGE,"E1.left");var subQ10=sQuery(id+"F0.wireOp",EDGE,"E23.filletArc");var subQ11=sQuery(id+"F0.wireOp",EDGE,"E24.filletArc");Q0=makeQuery(id+"F2.boolean.opBoolean","SPLIT",FACE,{"disambiguationData":[TD([makeQuery(id+"F1.opExtrude","SWEPT_FACE",FACE,{"disambiguationData":[OSD([subQ6])]})])],"derivedFrom":makeQuery(id+"F1.opExtrude","CAP_FACE",FACE,{"disambiguationData":[OSD([subQ6,subQ8,subQ9,subQ7,subQ4,subQ3,subQ2,subQ1,subQ0,subQ5,subQ10,subQ11])],"isStart":true})});}
            var sketch = newSketch(context, id + "F16", { "sketchPlane" : qUnion([Q0])});
            skLineSegment(sketch, "E79", {"start": v(0, 90) * mm, "end": v(0, 120) * mm});
            skLineSegment(sketch, "E80", {"start": v(-33, 90) * mm, "end": v(-15, 108) * mm});
            skLineSegment(sketch, "E81", {"start": v(33, 90) * mm, "end": v(15, 108) * mm});
            skLineSegment(sketch, "E82", {"start": v(15, 108) * mm, "end": v(15, 120) * mm});
            skLineSegment(sketch, "E83", {"start": v(-15, 108) * mm, "end": v(-15, 120) * mm});
            skArc(sketch, "E84", {"start": v(15, 120) * mm, "mid": v(0, 135) * mm, "end": v(-15, 120) * mm});
            skCircle(sketch, "E85", {"center": v(0, 120) * mm, "radius": 6 * mm});
            skArc(sketch, "E86.MirrorCS", {"start": v(-15, 120) * mm, "mid": v(0, 135) * mm, "end": v(15, 120) * mm});
            skLineSegment(sketch, "E87", {"start": v(-80, 0) * mm, "end": v(80, 0) * mm, "construction": true});
            skLineSegment(sketch, "E88.MirrorCS", {"start": v(-33, -90) * mm, "end": v(-15, -108) * mm});
            skLineSegment(sketch, "E89.MirrorCS", {"start": v(-15, -108) * mm, "end": v(-15, -120) * mm});
            skArc(sketch, "E90.MirrorCS", {"start": v(-15, -120) * mm, "mid": v(0, -135) * mm, "end": v(15, -120) * mm});
            skCircle(sketch, "E91.MirrorC", {"center": v(0, -120) * mm, "radius": 6 * mm});
            skLineSegment(sketch, "E92.MirrorCS", {"start": v(0, -90) * mm, "end": v(0, -120) * mm});
            skLineSegment(sketch, "E93.MirrorCS", {"start": v(15, -108) * mm, "end": v(15, -120) * mm});
            skLineSegment(sketch, "E94.MirrorCS", {"start": v(33, -90) * mm, "end": v(15, -108) * mm});
            skSolve(sketch);
        }
        {
            var Q0;
            {var subQ0=sQuery(id+"F16.wireOp",EDGE,"E88.MirrorCS");Q0=makeQuery(id+"F16.imprint","IMPRINT",FACE,{"disambiguationData":[TD([[makeQuery(id+"F16.imprint","IMPRINT",EDGE,{"derivedFrom":subQ0}),1.0]])]});}
            var Q1;
            Q1=makeQuery(id+"F16.imprint","IMPRINT",FACE,{"disambiguationData":[TD([[makeQuery(id+"F16.imprint","IMPRINT",EDGE,{"derivedFrom":makeQuery(id+"F1.opExtrude","CAP_EDGE",EDGE,{"disambiguationData":[OSD([sQuery(id+"F0.wireOp",EDGE,"E1.left")])],"isStart":true})}),-1.0]])]});
            var Q2;
            {var subQ2=sQuery(id+"F16.wireOp",EDGE,"E80");Q2=makeQuery(id+"F16.imprint","IMPRINT",FACE,{"disambiguationData":[TD([[makeQuery(id+"F16.imprint","IMPRINT",EDGE,{"derivedFrom":subQ2}),-1.0]])]});}
            var Q3;
            Q3=makeQuery(id+"F2.opExtrude","CAP_FACE",FACE,{"disambiguationData":[OSD([sQuery(id+"F0.wireOp",EDGE,"E12"),sQuery(id+"F0.wireOp",EDGE,"E13"),sQuery(id+"F0.wireOp",EDGE,"E14"),sQuery(id+"F0.wireOp",EDGE,"E15"),sQuery(id+"F0.wireOp",EDGE,"E17.filletArc"),sQuery(id+"F0.wireOp",EDGE,"E18.filletArc"),sQuery(id+"F0.wireOp",EDGE,"E19.filletArc"),sQuery(id+"F0.wireOp",EDGE,"E20.filletArc"),sQuery(id+"F0.wireOp",EDGE,"E25.0"),sQuery(id+"F0.wireOp",EDGE,"E25.1"),sQuery(id+"F0.wireOp",EDGE,"E25.2"),sQuery(id+"F0.wireOp",EDGE,"E25.3"),sQuery(id+"F0.wireOp",EDGE,"E25.4"),sQuery(id+"F0.wireOp",EDGE,"E25.5"),sQuery(id+"F0.wireOp",EDGE,"E25.6"),sQuery(id+"F0.wireOp",EDGE,"E25.7")])],"isStart":false});
            extrude(context, id + "F17", {"entities" : qUnion([Q0, Q1, Q2]), "endBound" : BoundingType.UP_TO_SURFACE, "depth" : -25 * mm, "endBoundEntityFace" : qUnion([Q3]), "offsetDistance" : 25 * mm});
        }
    });
